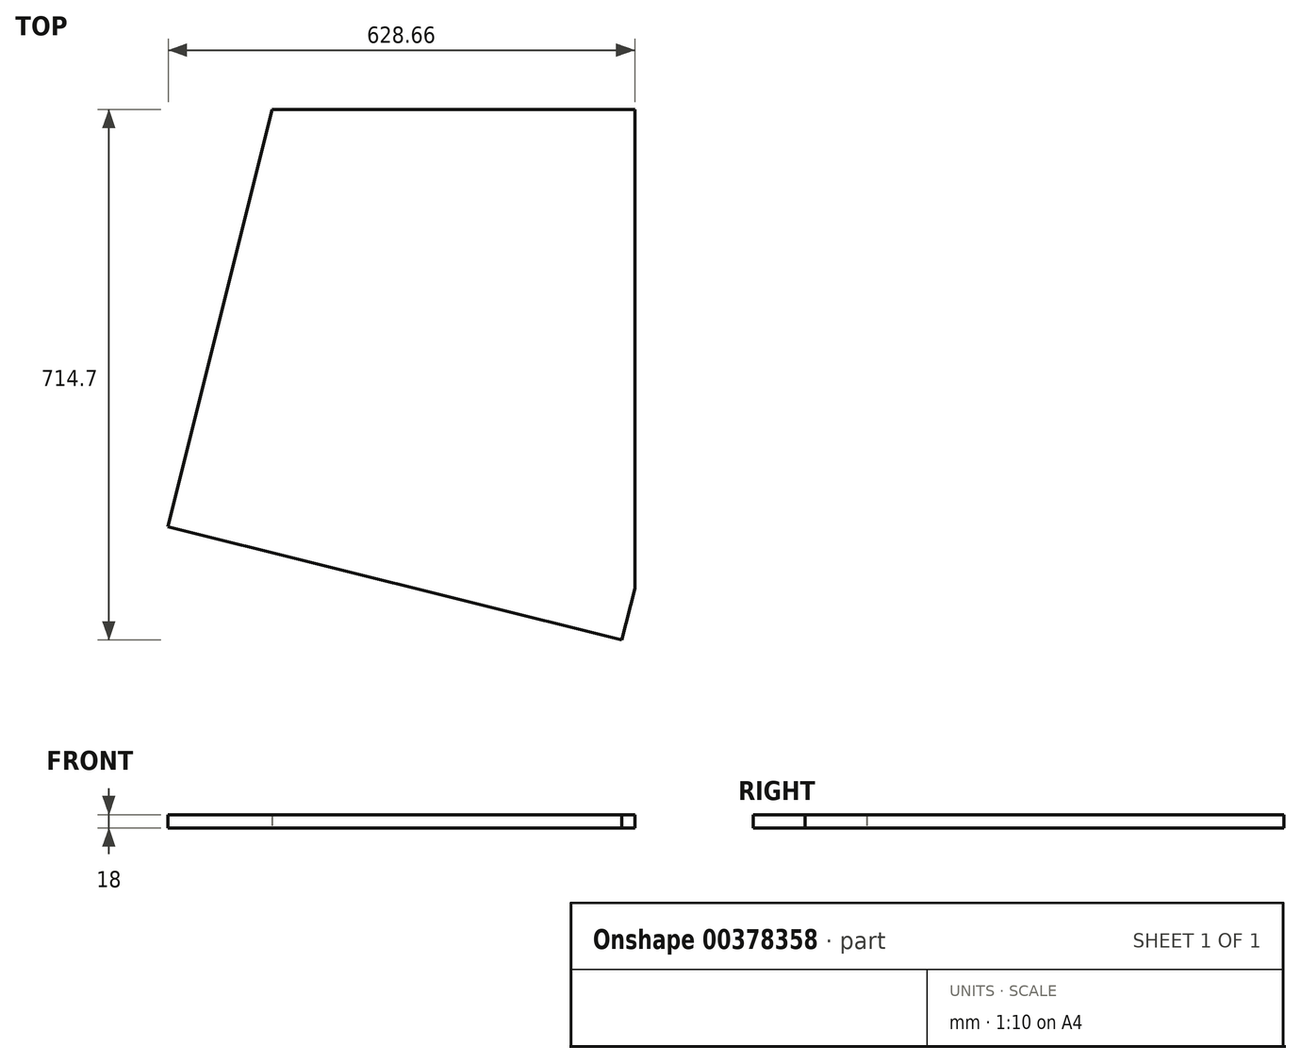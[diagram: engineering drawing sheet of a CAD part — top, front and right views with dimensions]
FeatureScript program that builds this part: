
annotation { "Feature Type Name" : "Feature", "Feature Type Description" : "" }
export const myFeature = defineFeature(function(context is Context, id is Id, definition is map)
    precondition{}
    {
        {
            var Q0;
            Q0=qCreatedBy(makeId("Top.planeOp"),FACE);
            var sketch = newSketch(context, id + "F0", { "sketchPlane" : qUnion([Q0])});
            skLineSegment(sketch, "E0", {"start": v(-343.47, 285) * mm, "end": v(145, 285) * mm});
            skLineSegment(sketch, "E1", {"start": v(145, -360) * mm, "end": v(127.62, -429.7) * mm});
            skLineSegment(sketch, "E2", {"start": v(127.62, -429.7) * mm, "end": v(-483.66, -277.29) * mm});
            skLineSegment(sketch, "E3", {"start": v(-483.66, -277.29) * mm, "end": v(-343.47, 285) * mm});
            skLineSegment(sketch, "E4", {"start": v(145, 285) * mm, "end": v(145, -360) * mm});
            skSolve(sketch);
        }
        {
            var Q0;
            Q0=qSketchRegion(id+"F0",true);
            extrude(context, id + "F1", {"entities" : qUnion([Q0]), "depth" : 18 * mm});
        }
    });
